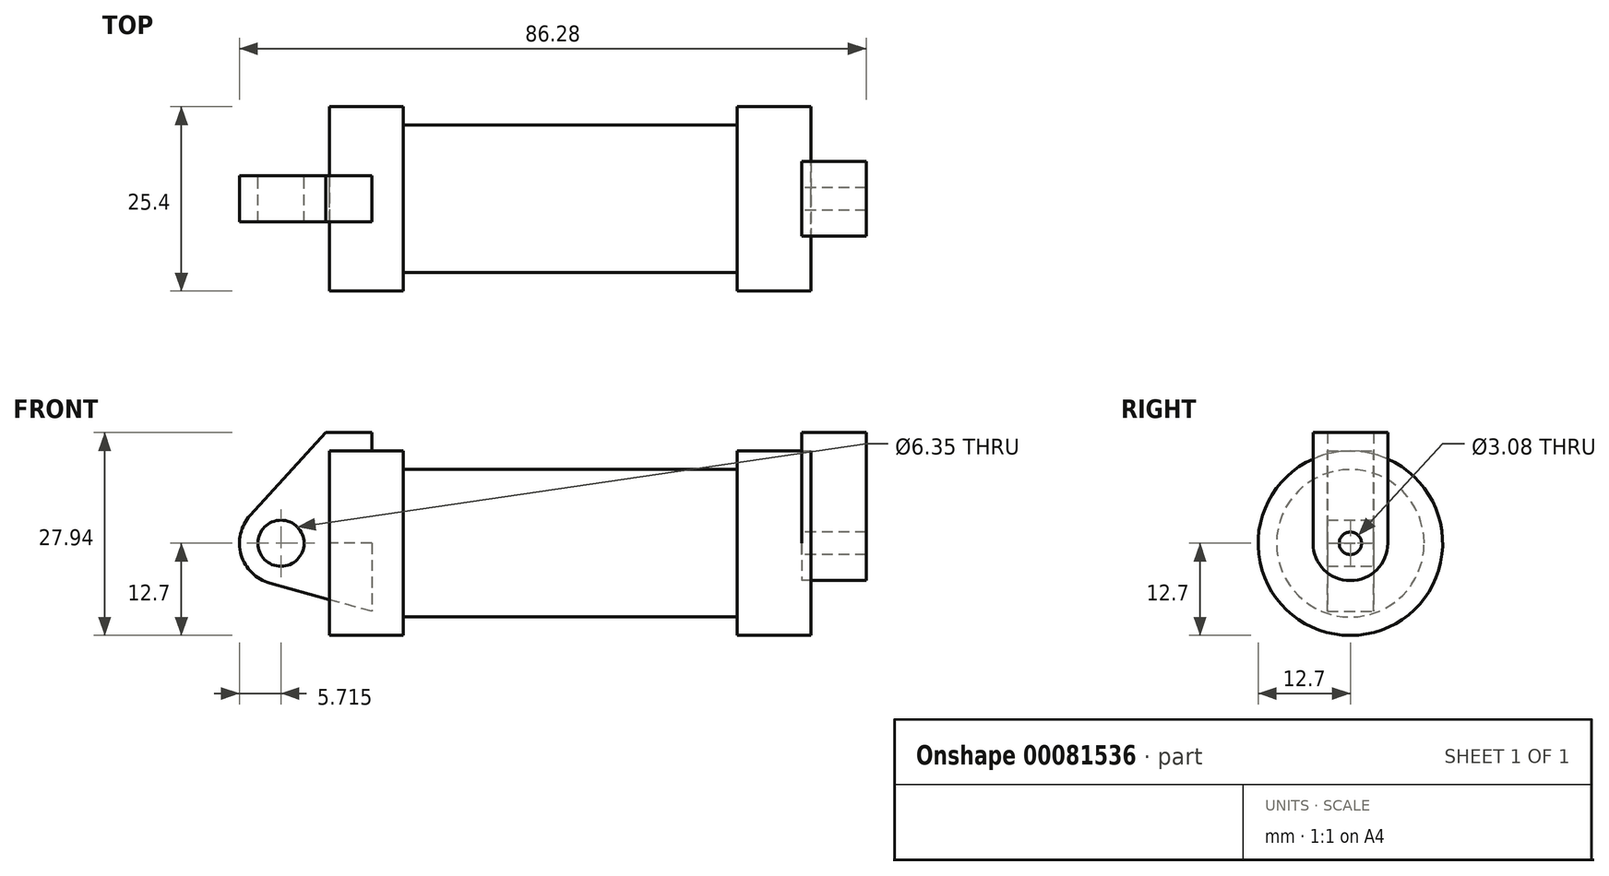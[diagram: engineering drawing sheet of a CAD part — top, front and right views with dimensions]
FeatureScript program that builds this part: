
annotation { "Feature Type Name" : "Feature", "Feature Type Description" : "" }
export const myFeature = defineFeature(function(context is Context, id is Id, definition is map)
    precondition{}
    {
        {
            var Q0;
            Q0=qCreatedBy(makeId("Front.planeOp"),FACE);
            var sketch = newSketch(context, id + "F0", { "sketchPlane" : qUnion([Q0])});
            skLineSegment(sketch, "E0", {"start": v(0, 0) * mm, "end": v(0, 12.7) * mm});
            skLineSegment(sketch, "E1", {"start": v(0, 12.7) * mm, "end": v(10.16, 12.7) * mm});
            skLineSegment(sketch, "E2", {"start": v(10.16, 12.7) * mm, "end": v(10.16, 10.16) * mm});
            skLineSegment(sketch, "E3", {"start": v(10.16, 10.16) * mm, "end": v(56.13, 10.16) * mm});
            skLineSegment(sketch, "E4", {"start": v(56.13, 10.16) * mm, "end": v(56.13, 12.7) * mm});
            skLineSegment(sketch, "E5", {"start": v(56.13, 12.7) * mm, "end": v(66.3, 12.7) * mm});
            skLineSegment(sketch, "E6", {"start": v(66.3, 12.7) * mm, "end": v(66.3, 0) * mm});
            skLineSegment(sketch, "E7", {"start": v(66.3, 0) * mm, "end": v(0, 0) * mm});
            skLineSegment(sketch, "E8", {"start": v(5.84, 15.24) * mm, "end": v(-0.5, 15.24) * mm});
            skLineSegment(sketch, "E9", {"start": v(-0.5, 15.24) * mm, "end": v(-10.88, 3.85) * mm});
            skLineSegment(sketch, "E10", {"start": v(0, 0) * mm, "end": v(-6.65, 0) * mm});
            skCircle(sketch, "E11", {"center": v(-6.65, 0) * mm, "radius": 5.72 * mm});
            skCircle(sketch, "E12", {"center": v(-6.65, 0) * mm, "radius": 3.18 * mm});
            skLineSegment(sketch, "E13", {"start": v(5.84, 15.24) * mm, "end": v(5.84, -9.4) * mm});
            skLineSegment(sketch, "E14", {"start": v(5.84, -9.4) * mm, "end": v(-8.18, -5.5) * mm});
            skSolve(sketch);
        }
        {
            var Q0;
            {var subQ0=sQuery(id+"F0.wireOp",EDGE,"E2");Q0=makeQuery(id+"F0.imprint","IMPRINT",FACE,{"disambiguationData":[TD([[makeQuery(id+"F0.imprint","IMPRINT",EDGE,{"derivedFrom":subQ0}),-1.0]])]});}
            var Q1;
            {var subQ0=sQuery(id+"F0.wireOp",EDGE,"E0");Q1=makeQuery(id+"F0.imprint","IMPRINT",FACE,{"disambiguationData":[TD([[makeQuery(id+"F0.imprint","IMPRINT",EDGE,{"derivedFrom":subQ0}),-1.0]])]});}
            var Q2;
            Q2=sQuery(id+"F0.wireOp",EDGE,"E7");
            revolve(context, id + "F1", {"entities" : qUnion([Q0, Q1]), "axis" : qUnion([Q2]), "revolveType" : RevolveType.FULL});
        }
        {
            var Q0;
            {var subQ3=sQuery(id+"F0.wireOp",EDGE,"E0");Q0=makeQuery(id+"F0.imprint","IMPRINT",FACE,{"disambiguationData":[TD([[makeQuery(id+"F0.imprint","IMPRINT",EDGE,{"derivedFrom":subQ3}),1.0]])]});}
            var Q1;
            {var subQ0=sQuery(id+"F0.wireOp",EDGE,"E14");Q1=makeQuery(id+"F0.imprint","IMPRINT",FACE,{"disambiguationData":[TD([[makeQuery(id+"F0.imprint","IMPRINT",EDGE,{"derivedFrom":subQ0}),-1.0]])]});}
            var Q2;
            {var subQ4=sQuery(id+"F0.wireOp",EDGE,"E12");Q2=makeQuery(id+"F0.imprint","IMPRINT",FACE,{"disambiguationData":[TD([[makeQuery(id+"F0.imprint","IMPRINT",EDGE,{"derivedFrom":subQ4}),-1.0]])]});}
            extrude(context, id + "F2", {"entities" : qUnion([Q0, Q1, Q2]), "endBound" : BoundingType.SYMMETRIC, "depth" : 6.35 * mm});
        }
        {
            var Q0;
            Q0=makeQuery(id+"F1.opRevolve","SWEPT_FACE",FACE,{"disambiguationData":[OSD([sQuery(id+"F0.wireOp",EDGE,"E6")])]});
            var sketch = newSketch(context, id + "F3", { "sketchPlane" : qUnion([Q0])});
            skCircle(sketch, "E15", {"center": v(0, 0) * mm, "radius": 1.54 * mm});
            skCircle(sketch, "E16", {"center": v(0, 0) * mm, "radius": 5.14 * mm});
            skLineSegment(sketch, "E17", {"start": v(-5.14, 0) * mm, "end": v(-5.14, 15.24) * mm});
            skLineSegment(sketch, "E18", {"start": v(5.14, 0) * mm, "end": v(5.14, 15.24) * mm});
            skLineSegment(sketch, "E19", {"start": v(-5.14, 15.24) * mm, "end": v(5.14, 15.24) * mm});
            skSolve(sketch);
        }
        {
            var Q0;
            Q0 = qSketchRegion(id + "F3", true);
            extrude(context, id + "F4", {"entities" : qUnion([Q0]), "depth" : 7.62 * mm, "hasSecondDirection" : true, "secondDirectionOppositeDirection" : true, "secondDirectionDepth" : 1.27 * mm});
        }
    });
